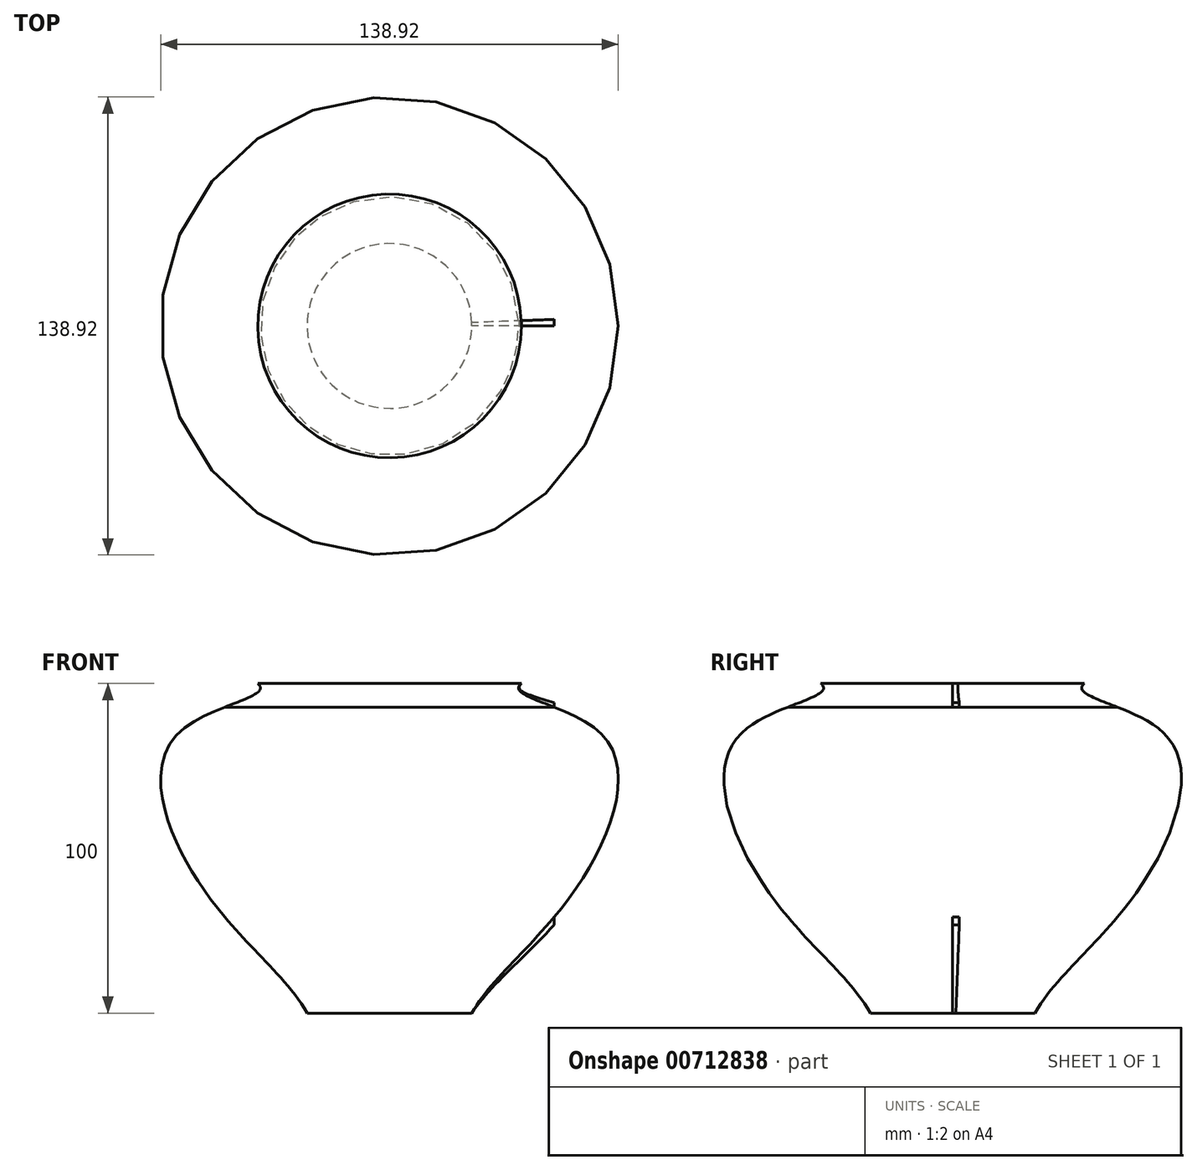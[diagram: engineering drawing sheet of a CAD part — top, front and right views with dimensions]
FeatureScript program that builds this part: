
annotation { "Feature Type Name" : "Feature", "Feature Type Description" : "" }
export const myFeature = defineFeature(function(context is Context, id is Id, definition is map)
    precondition{}
    {
        {
            assignVariable(context, id + "F0", {"name" : "ExtrusionWidth", "anyValue" : 0.8});
        }
        {
            assignVariable(context, id + "F1", {"name" : "TopDiameter", "anyValue" : 40});
        }
        {
            var Q0;
            Q0=qCreatedBy(makeId("Front.planeOp"),FACE);
            var sketch = newSketch(context, id + "F2", { "sketchPlane" : qUnion([Q0])});
            skLineSegment(sketch, "E0.bottom", {"start": v(0, 0) * mm, "end": v(50, 0) * mm});
            skLineSegment(sketch, "E0.top", {"start": v(0, 100) * mm, "end": v(50, 100) * mm});
            skLineSegment(sketch, "E0.left", {"start": v(0, 0) * mm, "end": v(0, 100) * mm});
            skLineSegment(sketch, "E0.right", {"start": v(50, 0) * mm, "end": v(50, 100) * mm});
            skFitSpline(sketch, "E1", {"points": [v(40, 100) * mm, v(63.88, 85.14) * mm, v(55.94, 36.8) * mm, v(25, 0) * mm], "startDerivative": vector(-56.57, -45.91) * mm, "endDerivative": vector(-51.53, -93.23) * mm});
            skFitSpline(sketch, "E2", {"points": [v(40.02, 100) * mm, v(65.1, 87.43) * mm, v(59.37, 38.57) * mm, v(25, 0) * mm], "startDerivative": vector(-51.28, -46.64) * mm, "endDerivative": vector(-58.76, -90.6) * mm});
            skSolve(sketch);
        }
        {
            var Q0;
            {var subQ0=sQuery(id+"F2.wireOp",EDGE,"E0.left");Q0=makeQuery(id+"F2.imprint","IMPRINT",FACE,{"disambiguationData":[TD([[makeQuery(id+"F2.imprint","IMPRINT",EDGE,{"derivedFrom":subQ0}),-1.0]])]});}
            var Q1;
            {var subQ0=sQuery(id+"F2.wireOp",EDGE,"E1");var subQ1=sQuery(id+"F2.wireOp",EDGE,"E0.right");var subQ2=makeQuery(id+"F2.imprint","INTERSECT",VERTEX,{"disambiguationData":[OD(0.0)],"derivedFrom":[subQ1,subQ0]});Q1=makeQuery(id+"F2.imprint","IMPRINT",FACE,{"disambiguationData":[TD([[makeQuery(id+"F2.imprint","IMPRINT",EDGE,{"disambiguationData":[TD([[subQ2,-1.0]])],"derivedFrom":subQ1}),-1.0]])]});}
            var Q2;
            Q2=sQuery(id+"F2.wireOp",EDGE,"E0.left");
            revolve(context, id + "F3", {"surfaceOperationType" : NewSurfaceOperationType.NEW, "entities" : qUnion([Q0, Q1]), "axis" : qUnion([Q2]), "revolveType" : RevolveType.FULL});
        }
        {
            var Q0;
            Q0=qCreatedBy(makeId("Top.planeOp"),FACE);
            var sketch = newSketch(context, id + "F4", { "sketchPlane" : qUnion([Q0])});
            skCircle(sketch, "E3.0", {"center": v(0, 0) * mm, "radius": 25 * mm});
            skLineSegment(sketch, "E4", {"start": v(25, 0) * mm, "end": v(35, 0) * mm});
            skLineSegment(sketch, "E5", {"start": v(35, 0) * mm, "end": v(34.96, -1.6) * mm});
            skLineSegment(sketch, "E6", {"start": v(34.96, -1.6) * mm, "end": v(24.97, -1.14) * mm});
            skSolve(sketch);
        }
        {
            var Q0;
            Q0=makeQuery(id+"F3.opRevolve","SWEPT_FACE",FACE,{"disambiguationData":[OSD([sQuery(id+"F2.wireOp",EDGE,"E0.top")])]});
            var sketch = newSketch(context, id + "F5", { "sketchPlane" : qUnion([Q0])});
            skCircle(sketch, "E7.0", {"center": v(0, 0) * mm, "radius": 40 * mm});
            skLineSegment(sketch, "E8", {"start": v(40, 0) * mm, "end": v(50, 0) * mm});
            skLineSegment(sketch, "E9", {"start": v(50, 0) * mm, "end": v(49.97, -1.6) * mm});
            skLineSegment(sketch, "E10", {"start": v(49.97, -1.6) * mm, "end": v(39.98, -1.28) * mm});
            skSolve(sketch);
        }
        {
            var Q0;
            {var subQ0=sQuery(id+"F2.wireOp",EDGE,"E1");Q0=makeQuery(id+"F2.imprint","IMPRINT",FACE,{"disambiguationData":[TD([[makeQuery(id+"F2.imprint","IMPRINT",EDGE,{"derivedFrom":subQ0}),1.0]])]});}
            var Q1;
            {var subQ0=sQuery(id+"F2.wireOp",EDGE,"E2");var subQ1=sQuery(id+"F2.wireOp",EDGE,"E0.right");var subQ2=makeQuery(id+"F2.imprint","INTERSECT",VERTEX,{"disambiguationData":[OD(0.0)],"derivedFrom":[subQ1,subQ0]});Q1=makeQuery(id+"F2.imprint","IMPRINT",FACE,{"disambiguationData":[TD([[makeQuery(id+"F2.imprint","IMPRINT",EDGE,{"disambiguationData":[TD([[subQ2,-1.0]])],"derivedFrom":subQ1}),-1.0]])]});}
            var Q2;
            {var subQ0=sQuery(id+"F2.wireOp",EDGE,"E1");var subQ1=sQuery(id+"F2.wireOp",EDGE,"E0.top");var subQ2=makeQuery(id+"F2.imprint","INTERSECT",VERTEX,{"derivedFrom":[subQ1,subQ0]});Q2=makeQuery(id+"F2.imprint","IMPRINT",FACE,{"disambiguationData":[TD([[makeQuery(id+"F2.imprint","IMPRINT",EDGE,{"disambiguationData":[TD([[subQ2,-1.0]])],"derivedFrom":subQ1}),-1.0]])]});}
            var Q3;
            Q3=sQuery(id+"F2.wireOp",EDGE,"E0.left");
            revolve(context, id + "F6", {"operationType" : NewBodyOperationType.ADD, "surfaceOperationType" : NewSurfaceOperationType.NEW, "entities" : qUnion([Q0, Q1, Q2]), "axis" : qUnion([Q3]), "revolveType" : RevolveType.ONE_DIRECTION, "angle" : ((getVariable(context, 'ExtrusionWidth') * 720) / (2 * PI * getVariable(context, 'TopDiameter'))) * degree});
        }
    });
